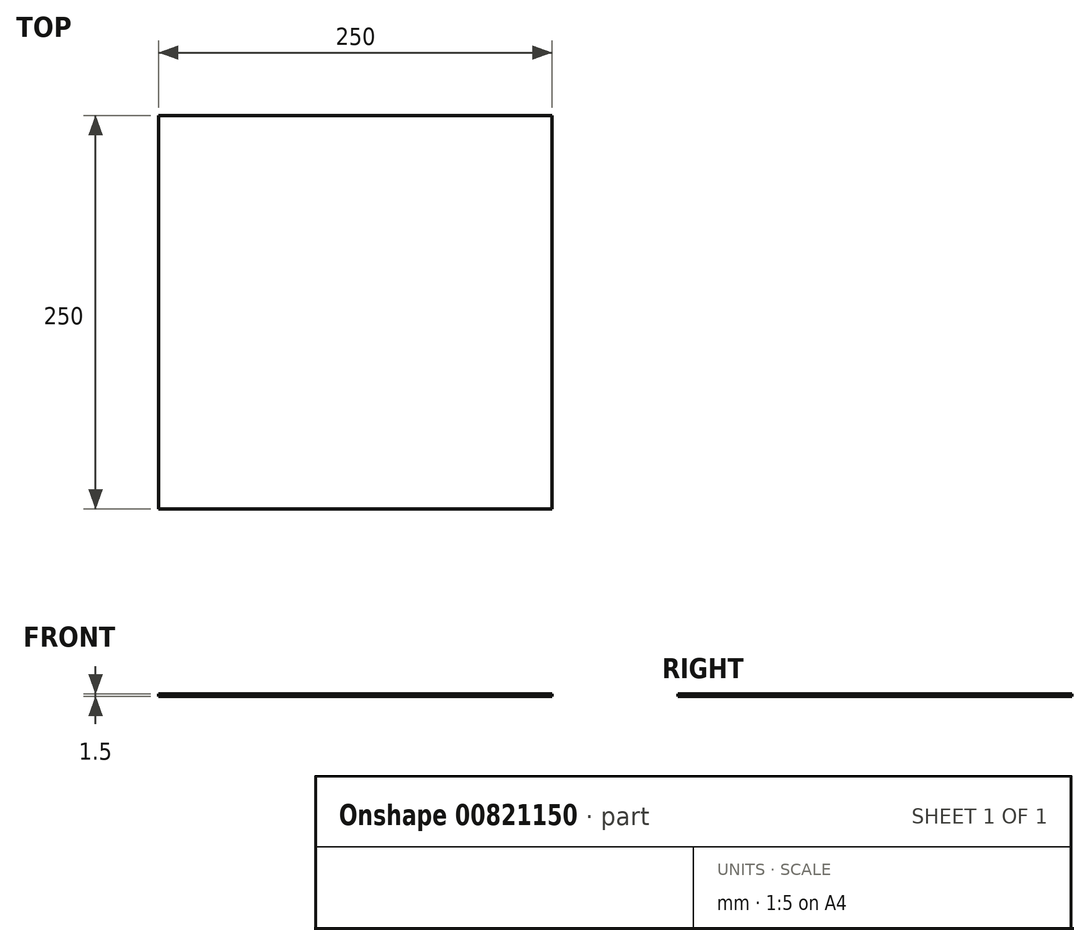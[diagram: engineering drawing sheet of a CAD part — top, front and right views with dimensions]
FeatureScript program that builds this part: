
annotation { "Feature Type Name" : "Feature", "Feature Type Description" : "" }
export const myFeature = defineFeature(function(context is Context, id is Id, definition is map)
    precondition{}
    {
        {
            var Q0;
            Q0=qCreatedBy(makeId("Top.planeOp"),FACE);
            var sketch = newSketch(context, id + "F0", { "sketchPlane" : qUnion([Q0])});
            skLineSegment(sketch, "E0.bottom", {"start": v(-47.86, 0) * mm, "end": v(202.14, 0) * mm});
            skLineSegment(sketch, "E0.top", {"start": v(-47.86, 250) * mm, "end": v(202.14, 250) * mm});
            skLineSegment(sketch, "E0.left", {"start": v(-47.86, 0) * mm, "end": v(-47.86, 250) * mm});
            skLineSegment(sketch, "E0.right", {"start": v(202.14, 0) * mm, "end": v(202.14, 250) * mm});
            skSolve(sketch);
        }
        {
            var Q0;
            Q0 = qSketchRegion(id + "F0", true);
            extrude(context, id + "F1", {"entities" : qUnion([Q0]), "depth" : 1.5 * mm, "offsetDistance" : 25 * mm});
        }
    });
